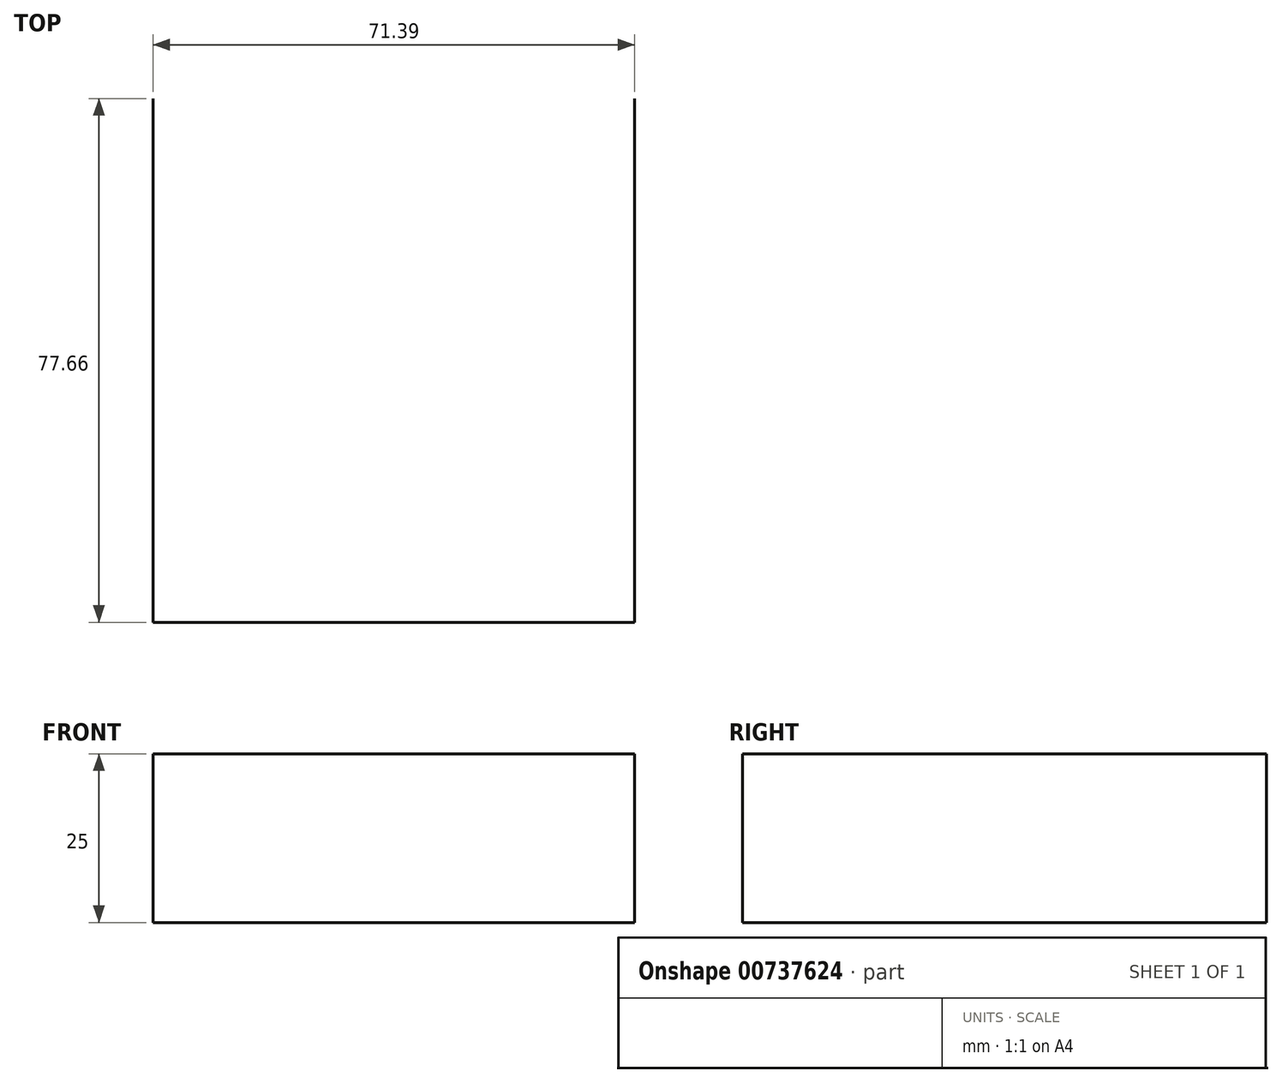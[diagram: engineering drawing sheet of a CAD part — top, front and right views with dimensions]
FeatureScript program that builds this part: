
annotation { "Feature Type Name" : "Feature", "Feature Type Description" : "" }
export const myFeature = defineFeature(function(context is Context, id is Id, definition is map)
    precondition{}
    {
        {
            var Q0;
            Q0=qCreatedBy(makeId("Top.planeOp"),FACE);
            var sketch = newSketch(context, id + "F0", { "sketchPlane" : qUnion([Q0])});
            skLineSegment(sketch, "E0.bottom", {"start": v(-41.19, -37.9) * mm, "end": v(30.2, -37.9) * mm});
            skLineSegment(sketch, "E0.top", {"start": v(-41.19, 39.77) * mm, "end": v(30.2, 39.77) * mm});
            skLineSegment(sketch, "E0.left", {"start": v(-41.19, -37.9) * mm, "end": v(-41.19, 39.77) * mm});
            skLineSegment(sketch, "E0.right", {"start": v(30.2, -37.9) * mm, "end": v(30.2, 39.77) * mm});
            skSolve(sketch);
        }
        {
            var Q0;
            Q0=sQuery(id+"F0.wireOp",EDGE,"E0.right");
            var Q1;
            Q1=sQuery(id+"F0.wireOp",EDGE,"E0.bottom");
            var Q2;
            Q2=sQuery(id+"F0.wireOp",EDGE,"E0.left");
            extrude(context, id + "F1", {"bodyType" : ToolBodyType.SURFACE, "surfaceEntities" : qUnion([Q0, Q1, Q2]), "depth" : 25 * mm, "offsetDistance" : 25 * mm});
        }
    });
